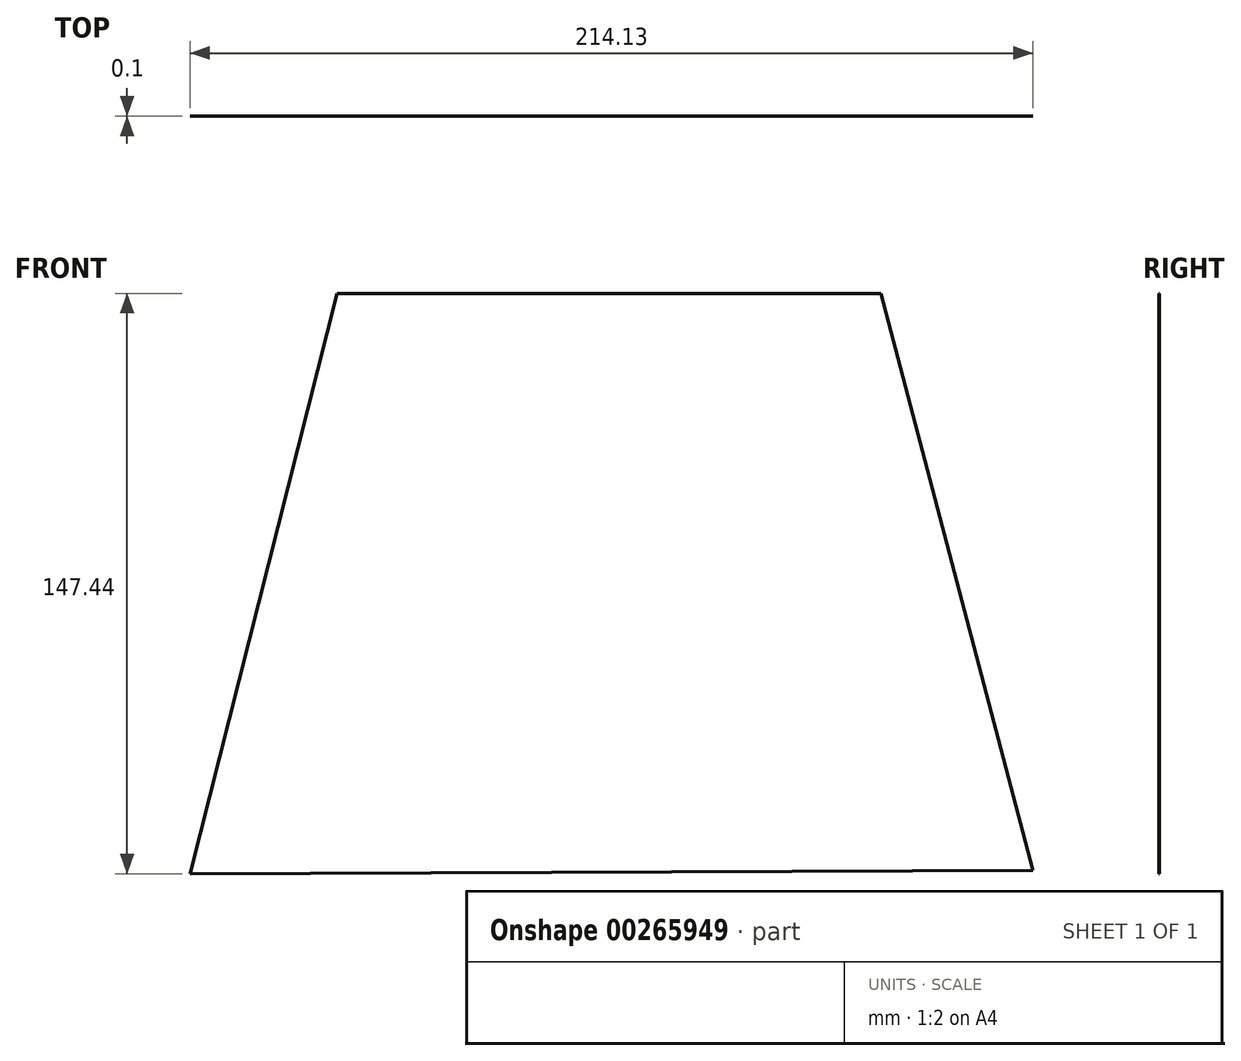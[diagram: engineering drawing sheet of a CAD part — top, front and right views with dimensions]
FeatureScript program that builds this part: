
annotation { "Feature Type Name" : "Feature", "Feature Type Description" : "" }
export const myFeature = defineFeature(function(context is Context, id is Id, definition is map)
    precondition{}
    {
        {
            var Q0;
            Q0=qCreatedBy(makeId("Front.planeOp"),FACE);
            var sketch = newSketch(context, id + "F0", { "sketchPlane" : qUnion([Q0])});
            skLineSegment(sketch, "E0", {"start": v(-64.5, 74.6) * mm, "end": v(73.72, 74.6) * mm});
            skLineSegment(sketch, "E1", {"start": v(-101.8, -72.84) * mm, "end": v(112.33, -71.96) * mm});
            skLineSegment(sketch, "E2", {"start": v(-64.5, 74.6) * mm, "end": v(-101.8, -72.84) * mm});
            skLineSegment(sketch, "E3", {"start": v(73.72, 74.6) * mm, "end": v(112.33, -71.96) * mm});
            skSolve(sketch);
        }
        {
            var Q0;
            Q0=makeQuery(id+"F0.imprint","IMPRINT",FACE,{"disambiguationData":[TD([[makeQuery(id+"F0.imprint","IMPRINT",EDGE,{"derivedFrom":sQuery(id+"F0.wireOp",EDGE,"E0")}),-1.0]])]});
            extrude(context, id + "F1", {"entities" : qUnion([Q0]), "depth" : 0.1 * mm});
        }
    });
